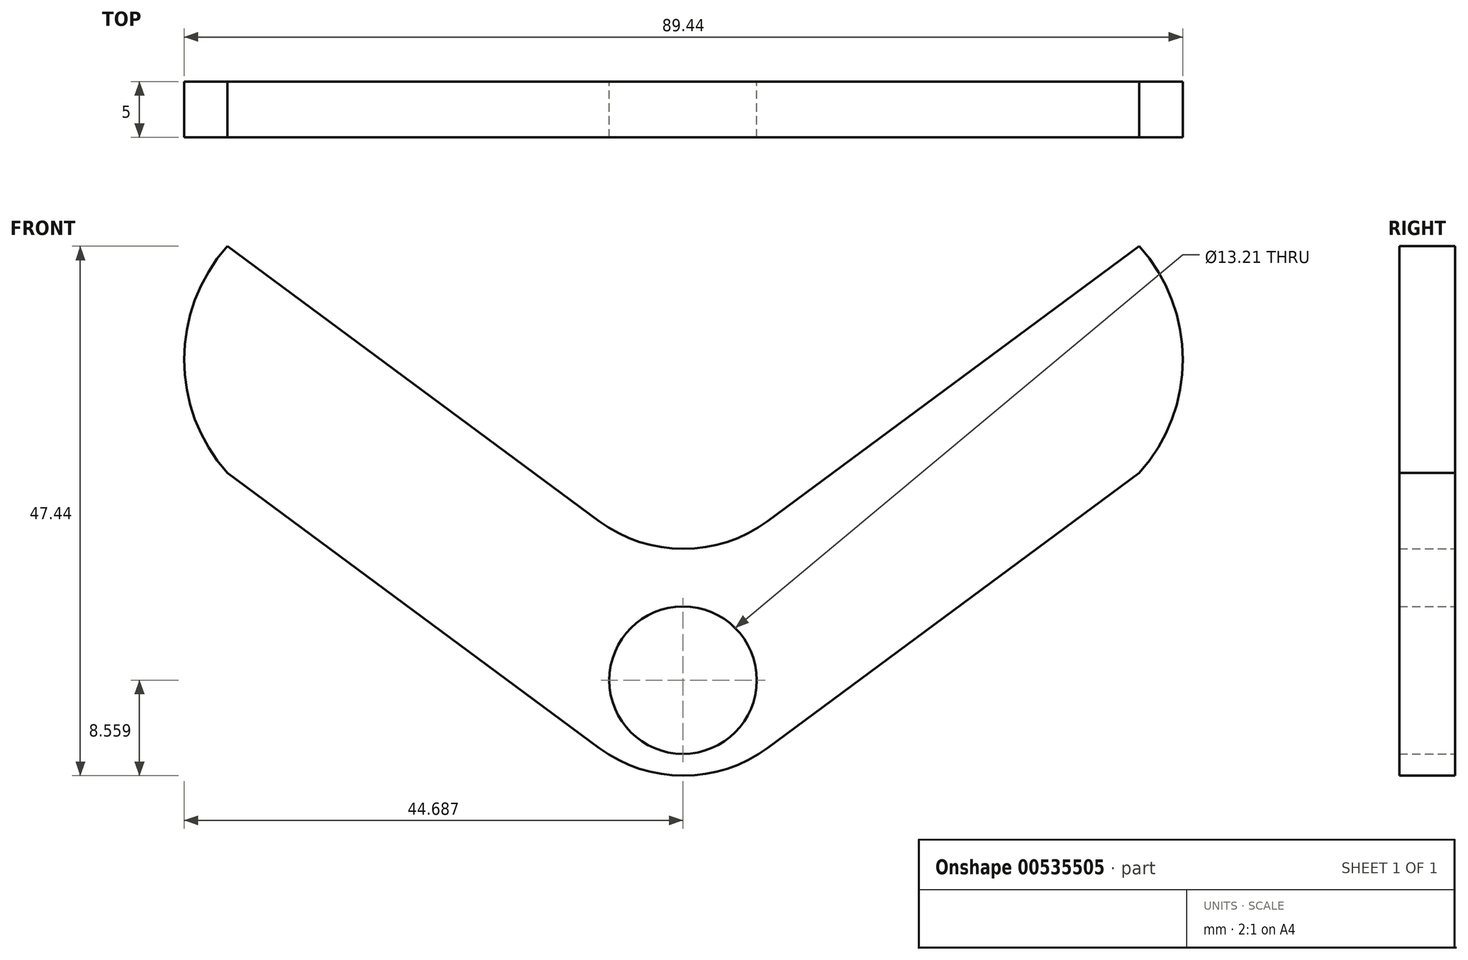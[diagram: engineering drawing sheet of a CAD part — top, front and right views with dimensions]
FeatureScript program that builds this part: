
annotation { "Feature Type Name" : "Feature", "Feature Type Description" : "" }
export const myFeature = defineFeature(function(context is Context, id is Id, definition is map)
    precondition{}
    {
        {
            var Q0;
            Q0=qCreatedBy(makeId("Front.planeOp"),FACE);
            var sketch = newSketch(context, id + "F0", { "sketchPlane" : qUnion([Q0])});
            skLineSegment(sketch, "E0", {"start": v(0, 0) * mm, "end": v(-40.84, 30.22) * mm});
            skLineSegment(sketch, "E1", {"start": v(0, 0) * mm, "end": v(40.84, 30.22) * mm});
            skLineSegment(sketch, "E2", {"start": v(0, 0) * mm, "end": v(0, -20.32) * mm});
            skLineSegment(sketch, "E3", {"start": v(0, -20.32) * mm, "end": v(-40.84, 9.9) * mm});
            skLineSegment(sketch, "E4", {"start": v(0, -20.32) * mm, "end": v(40.84, 9.9) * mm});
            skArc(sketch, "E5", {"start": v(-40.84, 30.22) * mm, "mid": v(-44.72, 20.06) * mm, "end": v(-40.84, 9.9) * mm});
            skArc(sketch, "E6", {"start": v(40.84, 9.9) * mm, "mid": v(44.72, 20.06) * mm, "end": v(40.84, 30.22) * mm});
            skCircle(sketch, "E7", {"center": v(-0.03, -8.66) * mm, "radius": 6.6 * mm});
            skSolve(sketch);
        }
        {
            var Q0;
            Q0 = qSketchRegion(id + "F0", true);
            extrude(context, id + "F1", {"entities" : qUnion([Q0]), "depth" : 5 * mm, "offsetDistance" : 25.4 * mm});
        }
        {
            var Q0;
            Q0=makeQuery(id+"F1.opExtrude","SWEPT_EDGE",EDGE,{"disambiguationData":[OSD([sQuery(id+"F0.wireOp",EDGE,"E2"),sQuery(id+"F0.wireOp",EDGE,"E3"),sQuery(id+"F0.wireOp",EDGE,"E4")])]});
            var Q1;
            Q1=makeQuery(id+"F1.opExtrude","SWEPT_EDGE",EDGE,{"disambiguationData":[OSD([sQuery(id+"F0.wireOp",EDGE,"E0"),sQuery(id+"F0.wireOp",EDGE,"E1"),sQuery(id+"F0.wireOp",EDGE,"E2")])]});
            fillet(context, id + "F2", {"entities" : qUnion([Q0, Q1]), "radius" : 12.7 * mm, "tangentPropagation" : true, "allowEdgeOverflow" : false});
        }
    });
